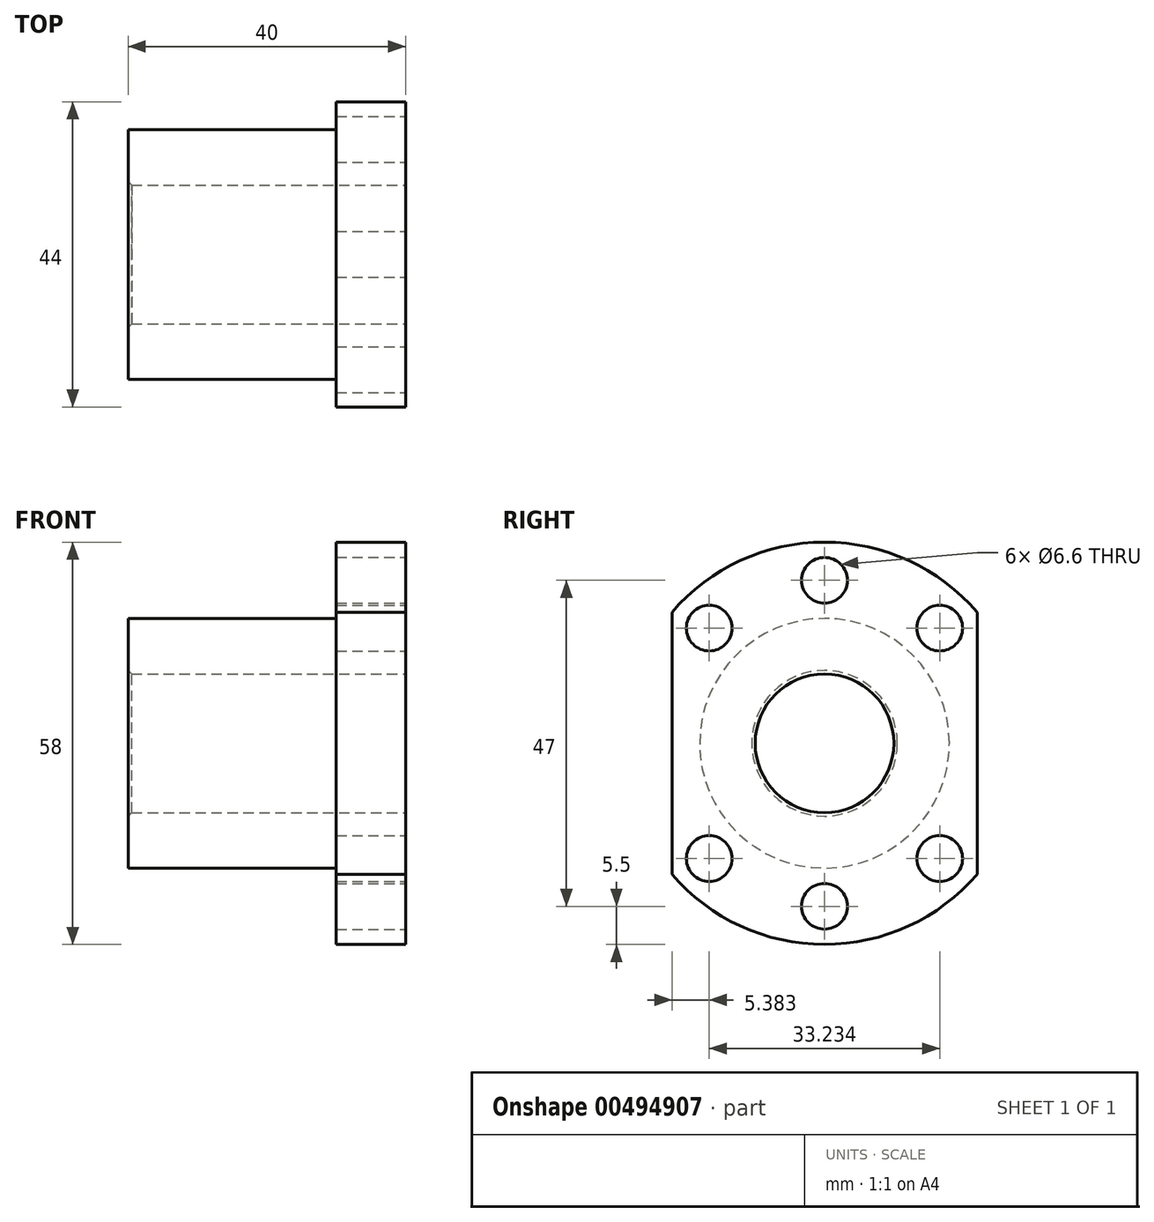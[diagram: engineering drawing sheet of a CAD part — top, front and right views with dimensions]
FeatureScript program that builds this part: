
annotation { "Feature Type Name" : "Feature", "Feature Type Description" : "" }
export const myFeature = defineFeature(function(context is Context, id is Id, definition is map)
    precondition{}
    {
        {
            var Q0;
            Q0=qCreatedBy(makeId("Right.planeOp"),FACE);
            var sketch = newSketch(context, id + "F0", { "sketchPlane" : qUnion([Q0])});
            skCircle(sketch, "E0", {"center": v(0, 0) * mm, "radius": 18 * mm});
            skSolve(sketch);
        }
        {
            var Q0;
            Q0=qSketchRegion(id+"F0",true);
            extrude(context, id + "F1", {"entities" : qUnion([Q0]), "oppositeDirection" : true, "depth" : 30 * mm});
        }
        {
            var Q0;
            Q0=makeQuery(id+"F1.opExtrude","CAP_FACE",FACE,{"disambiguationData":[OSD([sQuery(id+"F0.wireOp",EDGE,"E0")])],"isStart":true});
            var sketch = newSketch(context, id + "F2", { "sketchPlane" : qUnion([Q0])});
            skArc(sketch, "E1", {"start": v(-22, -18.9) * mm, "mid": v(0, -29) * mm, "end": v(22, -18.9) * mm});
            skLineSegment(sketch, "E2", {"start": v(-22, 18.9) * mm, "end": v(-22, -18.9) * mm});
            skLineSegment(sketch, "E3", {"start": v(22, 18.9) * mm, "end": v(22, -18.9) * mm});
            skPoint(sketch, "E4.orphan", {"position": v(-22, -42.3) * mm});
            skPoint(sketch, "E5.orphan", {"position": v(22, -42.3) * mm});
            skArc(sketch, "E6.trimOffspring", {"start": v(22, 18.9) * mm, "mid": v(0, 29) * mm, "end": v(-22, 18.9) * mm});
            skSolve(sketch);
        }
        {
            var Q0;
            Q0=qSketchRegion(id+"F2",true);
            extrude(context, id + "F3", {"entities" : qUnion([Q0]), "operationType" : NewBodyOperationType.ADD, "depth" : 10 * mm});
        }
        {
            var Q0;
            Q0=makeQuery(id+"F3.opExtrude","CAP_FACE",FACE,{"disambiguationData":[OSD([sQuery(id+"F2.wireOp",EDGE,"E1"),sQuery(id+"F2.wireOp",EDGE,"E2"),sQuery(id+"F2.wireOp",EDGE,"E3"),sQuery(id+"F2.wireOp",EDGE,"E6.trimOffspring")])],"isStart":false});
            var sketch = newSketch(context, id + "F4", { "sketchPlane" : qUnion([Q0])});
            skCircle(sketch, "E7", {"center": v(0, 0) * mm, "radius": 10 * mm});
            skSolve(sketch);
        }
        {
            var Q0;
            Q0=qSketchRegion(id+"F4",true);
            extrude(context, id + "F5", {"entities" : qUnion([Q0]), "operationType" : NewBodyOperationType.REMOVE, "endBound" : BoundingType.THROUGH_ALL, "oppositeDirection" : true, "depth" : 25 * mm});
        }
        {
            var Q0;
            Q0=makeQuery(id+"F5.boolean.opBoolean","COPY",EDGE,{"derivedFrom":makeQuery(id+"F5.opExtrude","CAP_EDGE",EDGE,{"disambiguationData":[OSD([sQuery(id+"F4.wireOp",EDGE,"E7")])],"isStart":true})});
            var Q1;
            Q1=makeQuery(id+"F5.boolean.opBoolean","INTERSECT",EDGE,{"derivedFrom":[makeQuery(id+"F1.opExtrude","CAP_FACE",FACE,{"disambiguationData":[OSD([sQuery(id+"F0.wireOp",EDGE,"E0")])],"isStart":false}),makeQuery(id+"F5.opExtrude","SWEPT_FACE",FACE,{"disambiguationData":[OSD([sQuery(id+"F4.wireOp",EDGE,"E7")])]})]});
            chamfer(context, id + "F6", {"entities" : qUnion([Q0, Q1]), "width" : 0.5 * mm, "tangentPropagation" : true});
        }
        {
            var Q0;
            Q0=makeQuery(id+"F3.opExtrude","CAP_FACE",FACE,{"disambiguationData":[OSD([sQuery(id+"F2.wireOp",EDGE,"E1"),sQuery(id+"F2.wireOp",EDGE,"E2"),sQuery(id+"F2.wireOp",EDGE,"E3"),sQuery(id+"F2.wireOp",EDGE,"E6.trimOffspring")])],"isStart":false});
            var sketch = newSketch(context, id + "F7", { "sketchPlane" : qUnion([Q0])});
            skPoint(sketch, "E8", {"position": v(0, 23.5) * mm});
            skPoint(sketch, "E9", {"position": v(0, -23.5) * mm});
            skPoint(sketch, "E10", {"position": v(16.62, -16.62) * mm});
            skPoint(sketch, "E11", {"position": v(-16.62, -16.62) * mm});
            skPoint(sketch, "E12", {"position": v(-16.62, 16.62) * mm});
            skPoint(sketch, "E13", {"position": v(16.62, 16.62) * mm});
            skSolve(sketch);
        }
        {
            var Q0;
            Q0=sQuery(id+"F7.wireOp",VERTEX,"E8");
            var Q1;
            Q1=sQuery(id+"F7.wireOp",VERTEX,"E13");
            var Q2;
            Q2=sQuery(id+"F7.wireOp",VERTEX,"E10");
            var Q3;
            Q3=sQuery(id+"F7.wireOp",VERTEX,"E9");
            var Q4;
            Q4=sQuery(id+"F7.wireOp",VERTEX,"E11");
            var Q5;
            Q5=sQuery(id+"F7.wireOp",VERTEX,"E12");
            var Q6;
            Q6=makeQuery(id+"F1.opExtrude","SWEPT_BODY",BODY,{"disambiguationData":[OSD([sQuery(id+"F0.wireOp",EDGE,"E0")])]});
            hole(context, id + "F8", {"style" : HoleStyle.SIMPLE, "endStyle" : HoleEndStyle.THROUGH, "standardTappedOrClearance" : lookupTablePath({ "standard" : "ISO", "size" : "6.6", "type" : "Drilled" }), "standardBlindInLast" : lookupTablePath({ "standard" : "ISO", "size" : "6.6", "type" : "Drilled" }), "holeDiameter" : 6.6 * mm, "isTappedThrough" : true, "tappedDepth" : 7.6 * mm, "tapClearance" : 3, "locations" : qUnion([Q0, Q1, Q2, Q3, Q4, Q5]), "scope" : qUnion([Q6])});
        }
    });
